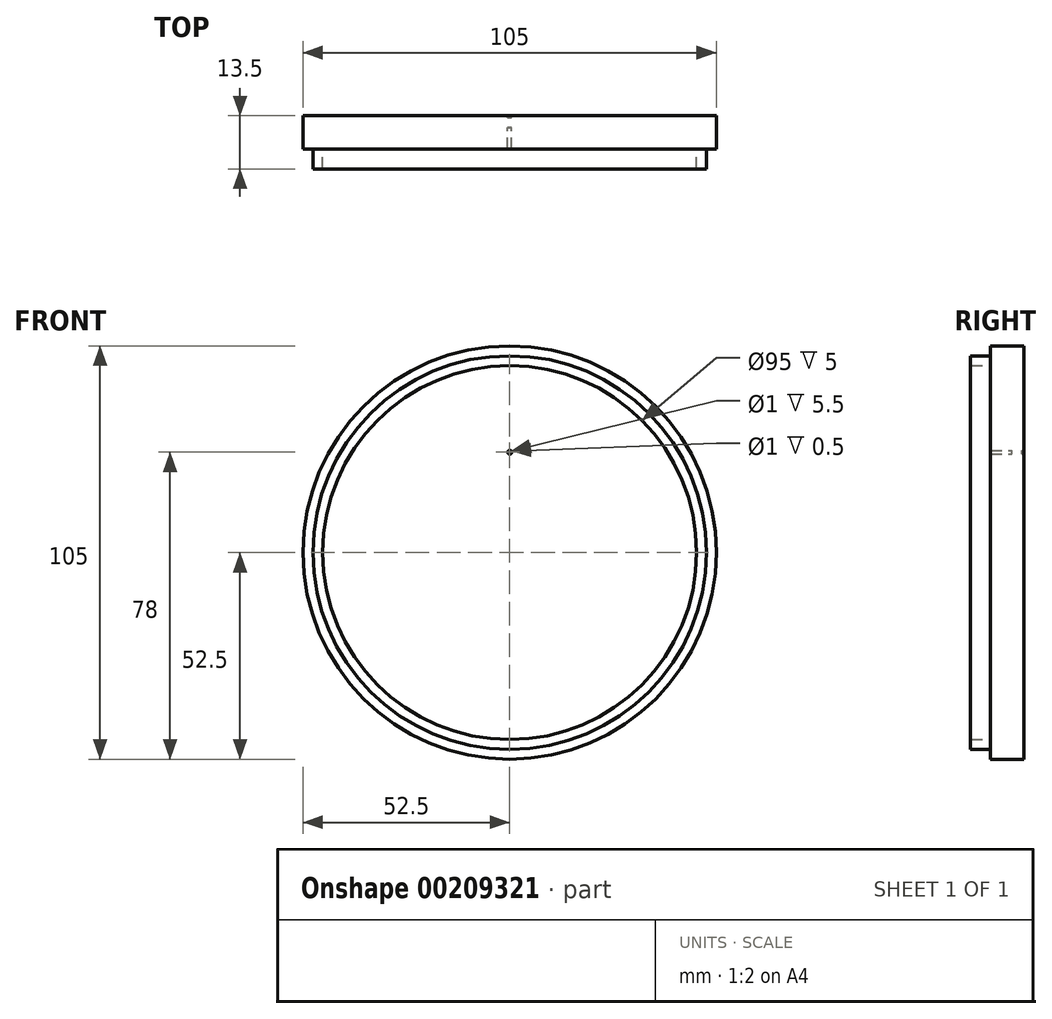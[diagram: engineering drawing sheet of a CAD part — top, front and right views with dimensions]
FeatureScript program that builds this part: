
annotation { "Feature Type Name" : "Feature", "Feature Type Description" : "" }
export const myFeature = defineFeature(function(context is Context, id is Id, definition is map)
    precondition{}
    {
        {
            var Q0;
            Q0=qCreatedBy(makeId("Front.planeOp"),FACE);
            var sketch = newSketch(context, id + "F0", { "sketchPlane" : qUnion([Q0])});
            skCircle(sketch, "E0", {"center": v(0, 0) * mm, "radius": 50 * mm});
            skSolve(sketch);
        }
        {
            var Q0;
            Q0=makeQuery(id+"F0.imprint","IMPRINT",FACE,{"disambiguationData":[TD([[makeQuery(id+"F0.imprint","IMPRINT",EDGE,{"derivedFrom":sQuery(id+"F0.wireOp",EDGE,"E0")}),1.0]])]});
            extrude(context, id + "F1", {"entities" : qUnion([Q0]), "depth" : 13 * mm});
        }
        {
            var Q0;
            Q0=makeQuery(id+"F1.opExtrude","CAP_FACE",FACE,{"disambiguationData":[OSD([sQuery(id+"F0.wireOp",EDGE,"E0")])],"isStart":false});
            shell(context, id + "F2", {"entities" : qUnion([Q0]), "thickness" : 2.5 * mm});
        }
        {
            var Q0;
            Q0=qCreatedBy(makeId("Front.planeOp"),FACE);
            var sketch = newSketch(context, id + "F3", { "sketchPlane" : qUnion([Q0])});
            skCircle(sketch, "E1", {"center": v(0, 25.5) * mm, "radius": 0.5 * mm});
            skCircle(sketch, "E2.0", {"center": v(0, 0) * mm, "radius": 52.5 * mm});
            skArc(sketch, "E3", {"start": v(0.42, -11.34) * mm, "mid": v(0.02, -10.94) * mm, "end": v(-0.38, -11.34) * mm});
            skArc(sketch, "E4.0", {"start": v(0.82, -11.35) * mm, "mid": v(0.02, -10.55) * mm, "end": v(-0.78, -11.35) * mm});
            skLineSegment(sketch, "E5", {"start": v(-0.78, -11.35) * mm, "end": v(-0.38, -11.35) * mm});
            skLineSegment(sketch, "E6", {"start": v(0.42, -11.35) * mm, "end": v(0.82, -11.35) * mm});
            skSolve(sketch);
        }
        {
            var Q0;
            Q0 = qSketchRegion(id + "F3", true);
            extrude(context, id + "F4", {"entities" : qUnion([Q0]), "operationType" : NewBodyOperationType.ADD, "depth" : 8 * mm});
        }
        {
            var Q0;
            Q0 = qSketchRegion(id + "F3", true);
            extrude(context, id + "F5", {"entities" : qUnion([Q0]), "operationType" : NewBodyOperationType.ADD, "endBound" : BoundingType.SYMMETRIC, "depth" : 1 * mm});
        }
    });
